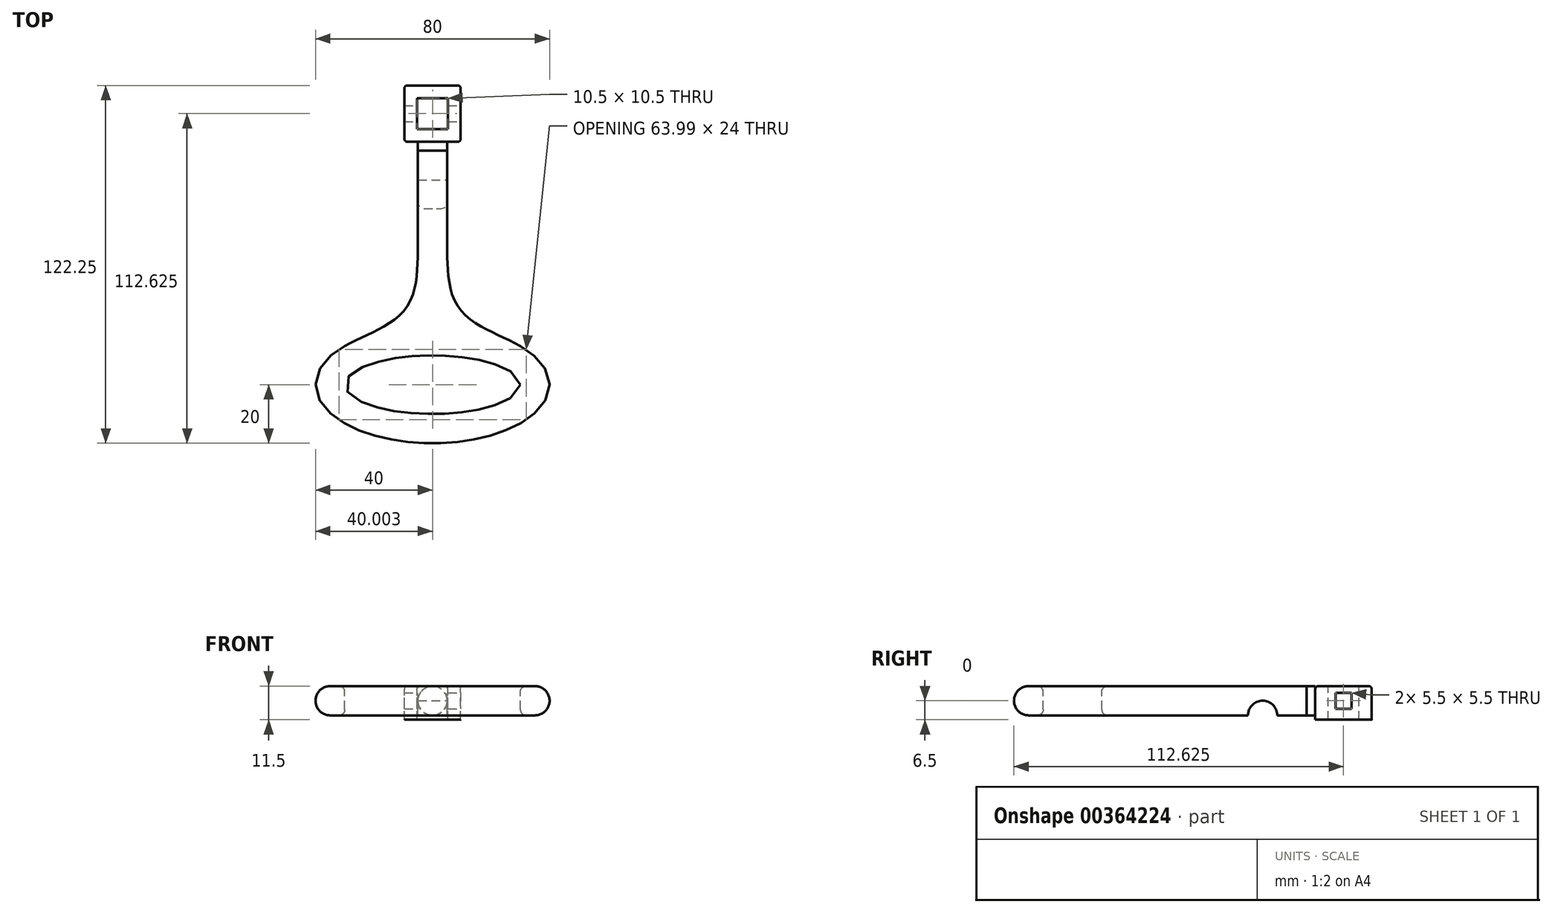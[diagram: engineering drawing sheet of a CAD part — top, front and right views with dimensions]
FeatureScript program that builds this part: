
annotation { "Feature Type Name" : "Feature", "Feature Type Description" : "" }
export const myFeature = defineFeature(function(context is Context, id is Id, definition is map)
    precondition{}
    {
        {
            var Q0;
            Q0=qCreatedBy(makeId("Front.planeOp"),FACE);
            var sketch = newSketch(context, id + "F0", { "sketchPlane" : qUnion([Q0])});
            skLineSegment(sketch, "E0.bottom", {"start": v(5, 5) * mm, "end": v(-5, 5) * mm});
            skLineSegment(sketch, "E0.top", {"start": v(5, -5) * mm, "end": v(-5, -5) * mm});
            skLineSegment(sketch, "E0.left", {"start": v(5, 5) * mm, "end": v(5, -5) * mm});
            skLineSegment(sketch, "E0.right", {"start": v(-5, 5) * mm, "end": v(-5, -5) * mm});
            skPoint(sketch, "E0.middle", {"position": v(0, 0) * mm});
            skSolve(sketch);
        }
        {
            var Q0;
            Q0=makeQuery(id+"F0.imprint","IMPRINT",FACE,{"disambiguationData":[TD([[makeQuery(id+"F0.imprint","IMPRINT",EDGE,{"derivedFrom":sQuery(id+"F0.wireOp",EDGE,"E0.bottom")}),1.0]])]});
            extrude(context, id + "F1", {"entities" : qUnion([Q0]), "oppositeDirection" : true, "depth" : 30 * mm});
        }
        {
            var Q0;
            Q0=makeQuery(id+"F1.opExtrude","SWEPT_FACE",FACE,{"disambiguationData":[OSD([sQuery(id+"F0.wireOp",EDGE,"E0.bottom")])]});
            var sketch = newSketch(context, id + "F2", { "sketchPlane" : qUnion([Q0])});
            skPoint(sketch, "E1", {"position": v(0, 42.62) * mm});
            skLineSegment(sketch, "E2.bottom", {"start": v(8.62, 52.25) * mm, "end": v(-8.63, 52.25) * mm});
            skLineSegment(sketch, "E2.top", {"start": v(8.62, 33) * mm, "end": v(-8.63, 33) * mm});
            skLineSegment(sketch, "E2.left", {"start": v(9.62, 51.25) * mm, "end": v(9.62, 34) * mm});
            skLineSegment(sketch, "E2.right", {"start": v(-9.63, 51.25) * mm, "end": v(-9.63, 34) * mm});
            skPoint(sketch, "E3.visualSharp", {"position": v(-9.63, 52.25) * mm});
            skArc(sketch, "E3.filletArc", {"start": v(-8.63, 52.25) * mm, "mid": v(-9.33, 51.96) * mm, "end": v(-9.63, 51.25) * mm});
            skPoint(sketch, "E4.visualSharp", {"position": v(9.62, 52.25) * mm});
            skArc(sketch, "E4.filletArc", {"start": v(9.62, 51.25) * mm, "mid": v(9.33, 51.96) * mm, "end": v(8.62, 52.25) * mm});
            skPoint(sketch, "E5.visualSharp", {"position": v(9.62, 33) * mm});
            skArc(sketch, "E5.filletArc", {"start": v(8.62, 33) * mm, "mid": v(9.33, 33.3) * mm, "end": v(9.62, 34) * mm});
            skPoint(sketch, "E6.visualSharp", {"position": v(-9.63, 33) * mm});
            skArc(sketch, "E6.filletArc", {"start": v(-9.63, 34) * mm, "mid": v(-9.33, 33.3) * mm, "end": v(-8.63, 33) * mm});
            skLineSegment(sketch, "E7.bottom", {"start": v(5.25, 47.88) * mm, "end": v(-5.25, 47.88) * mm});
            skLineSegment(sketch, "E7.top", {"start": v(5.25, 37.38) * mm, "end": v(-5.25, 37.38) * mm});
            skLineSegment(sketch, "E7.left", {"start": v(5.25, 47.88) * mm, "end": v(5.25, 37.38) * mm});
            skLineSegment(sketch, "E7.right", {"start": v(-5.25, 47.88) * mm, "end": v(-5.25, 37.38) * mm});
            skSolve(sketch);
        }
        {
            var Q0;
            Q0=makeQuery(id+"F2.imprint","IMPRINT",FACE,{"disambiguationData":[TD([[makeQuery(id+"F2.imprint","IMPRINT",EDGE,{"derivedFrom":sQuery(id+"F2.wireOp",EDGE,"E2.bottom")}),1.0]])]});
            extrude(context, id + "F3", {"entities" : qUnion([Q0]), "oppositeDirection" : true, "depth" : 11.5 * mm});
        }
        {
            var Q0;
            Q0=makeQuery(id+"F1.opExtrude","SWEPT_FACE",FACE,{"disambiguationData":[OSD([sQuery(id+"F0.wireOp",EDGE,"E0.bottom")])]});
            var sketch = newSketch(context, id + "F4", { "sketchPlane" : qUnion([Q0])});
            skLineSegment(sketch, "E8.bottom", {"start": v(-5, 30) * mm, "end": v(5, 30) * mm});
            skLineSegment(sketch, "E8.top", {"start": v(-5, 33) * mm, "end": v(5, 33) * mm});
            skLineSegment(sketch, "E8.left", {"start": v(-5, 30) * mm, "end": v(-5, 33) * mm});
            skLineSegment(sketch, "E8.right", {"start": v(5, 30) * mm, "end": v(5, 33) * mm});
            skSolve(sketch);
        }
        {
            var Q0;
            Q0=makeQuery(id+"F4.imprint","IMPRINT",FACE,{"disambiguationData":[TD([[makeQuery(id+"F4.imprint","IMPRINT",EDGE,{"derivedFrom":sQuery(id+"F4.wireOp",EDGE,"E8.bottom")}),-1.0]])]});
            extrude(context, id + "F5", {"entities" : qUnion([Q0]), "oppositeDirection" : true, "depth" : 10 * mm});
        }
        {
            var Q0;
            Q0=makeQuery(id+"F3.opExtrude","SWEPT_FACE",FACE,{"disambiguationData":[OSD([sQuery(id+"F2.wireOp",EDGE,"E2.left")])]});
            var sketch = newSketch(context, id + "F6", { "sketchPlane" : qUnion([Q0])});
            skPoint(sketch, "E9", {"position": v(42.62, 0) * mm});
            skLineSegment(sketch, "E10.bottom", {"start": v(45.37, 2.75) * mm, "end": v(39.87, 2.75) * mm});
            skLineSegment(sketch, "E10.top", {"start": v(45.37, -2.75) * mm, "end": v(39.87, -2.75) * mm});
            skLineSegment(sketch, "E10.left", {"start": v(45.37, 2.75) * mm, "end": v(45.37, -2.75) * mm});
            skLineSegment(sketch, "E10.right", {"start": v(39.87, 2.75) * mm, "end": v(39.87, -2.75) * mm});
            skSolve(sketch);
        }
        {
            var Q0;
            Q0=makeQuery(id+"F6.imprint","IMPRINT",FACE,{"disambiguationData":[TD([[makeQuery(id+"F6.imprint","IMPRINT",EDGE,{"derivedFrom":sQuery(id+"F6.wireOp",EDGE,"E10.bottom")}),1.0]])]});
            extrude(context, id + "F7", {"entities" : qUnion([Q0]), "operationType" : NewBodyOperationType.REMOVE, "endBound" : BoundingType.THROUGH_ALL, "oppositeDirection" : true, "depth" : 25 * mm});
        }
        {
            var Q0;
            Q0=makeQuery(id+"F1.opExtrude","SWEPT_FACE",FACE,{"disambiguationData":[OSD([sQuery(id+"F0.wireOp",EDGE,"E0.left")])]});
            var sketch = newSketch(context, id + "F8", { "sketchPlane" : qUnion([Q0])});
            skPoint(sketch, "E11", {"position": v(20, -5) * mm});
            skPoint(sketch, "E12", {"position": v(10, -5) * mm});
            skPoint(sketch, "E13", {"position": v(15, 0) * mm});
            skArc(sketch, "E14", {"start": v(20, -5) * mm, "mid": v(15, 0) * mm, "end": v(10, -5) * mm});
            skSolve(sketch);
        }
        {
            var Q0;
            {var subQ0=sQuery(id+"F8.wireOp",EDGE,"E14");Q0=makeQuery(id+"F8.imprint","IMPRINT",FACE,{"disambiguationData":[TD([[makeQuery(id+"F8.imprint","IMPRINT",EDGE,{"derivedFrom":subQ0}),1.0]])]});}
            extrude(context, id + "F9", {"entities" : qUnion([Q0]), "operationType" : NewBodyOperationType.REMOVE, "endBound" : BoundingType.THROUGH_ALL, "oppositeDirection" : true, "depth" : 25 * mm});
        }
        {
            var Q0;
            Q0=makeQuery(id+"F3.opExtrude","CAP_EDGE",EDGE,{"disambiguationData":[OSD([sQuery(id+"F2.wireOp",EDGE,"E2.right")])],"isStart":true});
            fillet(context, id + "F10", {"entities" : qUnion([Q0]), "radius" : 1 * mm, "tangentPropagation" : true, "allowEdgeOverflow" : false});
        }
        {
            var Q0;
            Q0=qCreatedBy(makeId("Top.planeOp"),FACE);
            var sketch = newSketch(context, id + "F11", { "sketchPlane" : qUnion([Q0])});
            skPoint(sketch, "E15", {"position": v(0, -50) * mm});
            skEllipse(sketch, "E16", {"center": v(0, -50) * mm, "majorRadius": 40 * mm, "minorRadius": 20 * mm, "majorAxis": v(1, 0)});
            skEllipse(sketch, "E17", {"center": v(0, -50) * mm, "majorRadius": 30 * mm, "minorRadius": 10 * mm, "majorAxis": v(1, 0)});
            skLineSegment(sketch, "E18", {"start": v(-30, -50) * mm, "end": v(-40, -50) * mm});
            skLineSegment(sketch, "E19", {"start": v(30, -50) * mm, "end": v(40, -50) * mm});
            skPoint(sketch, "E20", {"position": v(-5, 0) * mm});
            skPoint(sketch, "E21", {"position": v(5, 0) * mm});
            skFitSpline(sketch, "E22", {"points": [v(-5, 0) * mm, v(-10, -25) * mm, v(-30, -36.77) * mm], "startDerivative": vector(0, -63.9) * mm, "endDerivative": vector(-36.8, -20.87) * mm});
            skFitSpline(sketch, "E23", {"points": [v(5, 0) * mm, v(10, -25) * mm, v(30, -36.77) * mm], "startDerivative": vector(0, -63.9) * mm, "endDerivative": vector(35.52, -20.14) * mm});
            skLineSegment(sketch, "E24", {"start": v(-5, 0) * mm, "end": v(5, 0) * mm});
            skSolve(sketch);
        }
        {
            var Q0;
            {var subQ0=sQuery(id+"F11.wireOp",EDGE,"E22");Q0=makeQuery(id+"F11.imprint","IMPRINT",FACE,{"disambiguationData":[TD([[makeQuery(id+"F11.imprint","IMPRINT",EDGE,{"derivedFrom":subQ0}),1.0]])]});}
            var Q1;
            {var subQ0=sQuery(id+"F11.wireOp",EDGE,"E18");Q1=makeQuery(id+"F11.imprint","IMPRINT",FACE,{"disambiguationData":[TD([[makeQuery(id+"F11.imprint","IMPRINT",EDGE,{"derivedFrom":subQ0}),-1.0]])]});}
            var Q2;
            {var subQ0=sQuery(id+"F11.wireOp",EDGE,"E18");Q2=makeQuery(id+"F11.imprint","IMPRINT",FACE,{"disambiguationData":[TD([[makeQuery(id+"F11.imprint","IMPRINT",EDGE,{"derivedFrom":subQ0}),1.0]])]});}
            extrude(context, id + "F12", {"entities" : qUnion([Q0, Q1, Q2]), "operationType" : NewBodyOperationType.ADD, "endBound" : BoundingType.SYMMETRIC, "oppositeDirection" : true, "depth" : 10 * mm});
        }
        {
            var Q0;
            Q0=makeQuery(id+"F12.opExtrude","CAP_EDGE",EDGE,{"disambiguationData":[OSD([sQuery(id+"F11.wireOp",EDGE,"E16")])],"isStart":true});
            fillet(context, id + "F13", {"entities" : qUnion([Q0]), "radius" : 5 * mm, "tangentPropagation" : true, "allowEdgeOverflow" : false});
        }
        {
            var Q0;
            Q0=makeQuery(id+"F12.opExtrude","CAP_EDGE",EDGE,{"disambiguationData":[OSD([sQuery(id+"F11.wireOp",EDGE,"E16")])],"isStart":false});
            fillet(context, id + "F14", {"entities" : qUnion([Q0]), "radius" : 5 * mm, "tangentPropagation" : true, "allowEdgeOverflow" : false});
        }
        {
            var Q0;
            Q0=makeQuery(id+"F12.opExtrude","CAP_EDGE",EDGE,{"disambiguationData":[OSD([sQuery(id+"F11.wireOp",EDGE,"E17")])],"isStart":true});
            var Q1;
            Q1=makeQuery(id+"F12.opExtrude","CAP_EDGE",EDGE,{"disambiguationData":[OSD([sQuery(id+"F11.wireOp",EDGE,"E17")])],"isStart":false});
            fillet(context, id + "F15", {"entities" : qUnion([Q0, Q1]), "radius" : 2 * mm, "tangentPropagation" : true, "allowEdgeOverflow" : false});
        }
    });
